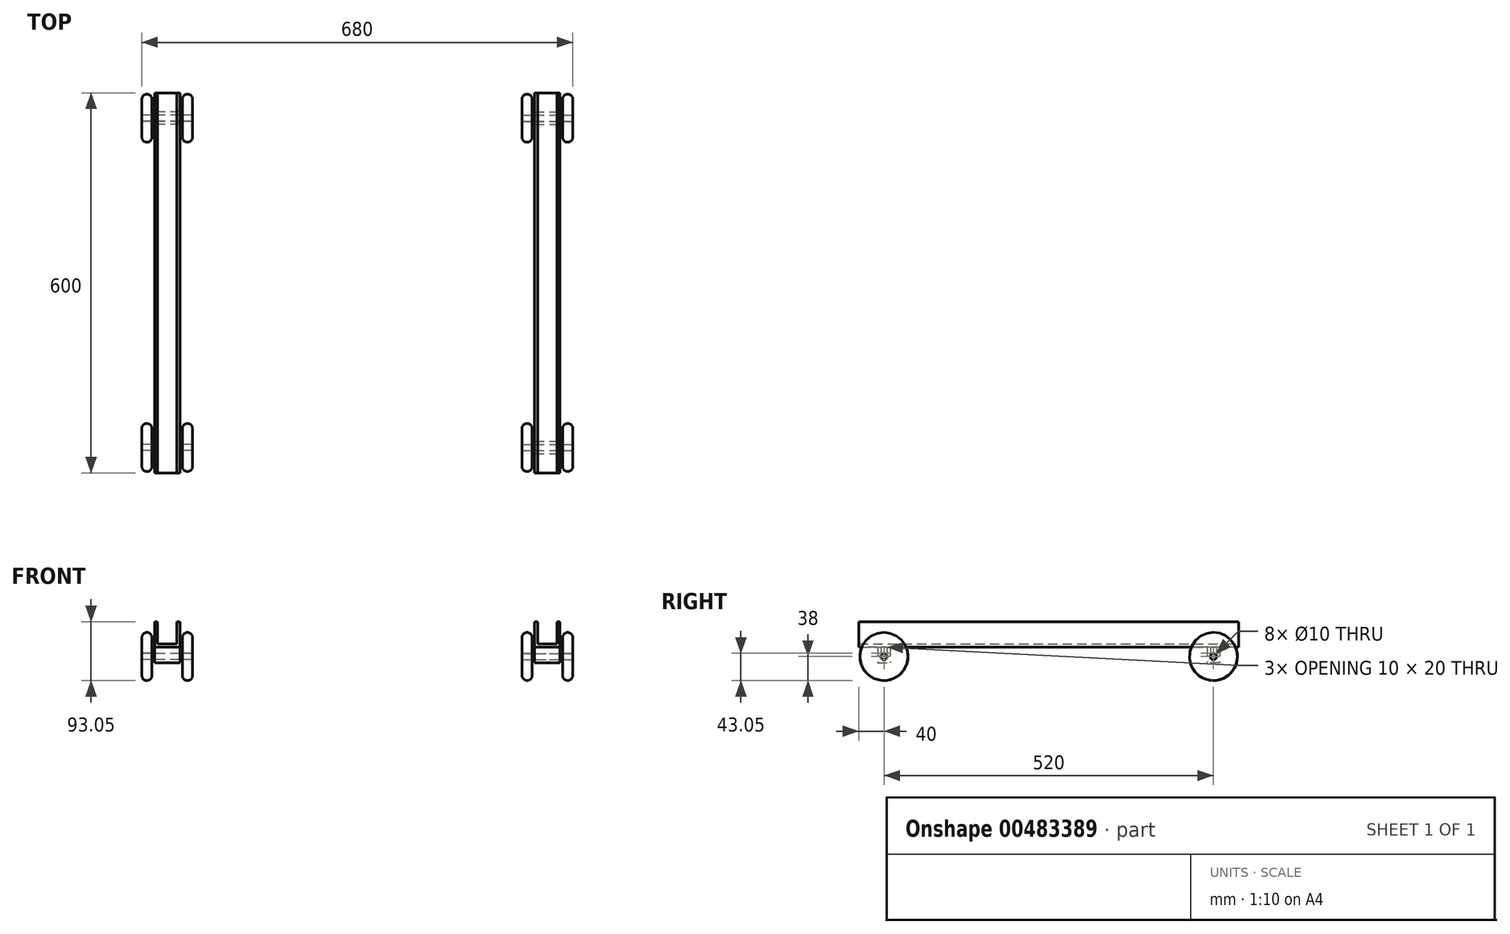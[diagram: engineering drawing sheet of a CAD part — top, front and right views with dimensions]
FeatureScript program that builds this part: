
annotation { "Feature Type Name" : "Feature", "Feature Type Description" : "" }
export const myFeature = defineFeature(function(context is Context, id is Id, definition is map)
    precondition{}
    {
        {
            var Q0;
            Q0=qCreatedBy(makeId("Front.planeOp"),FACE);
            var sketch = newSketch(context, id + "F0", { "sketchPlane" : qUnion([Q0])});
            skLineSegment(sketch, "E0", {"start": v(0, 0) * mm, "end": v(-280, 0) * mm, "construction": true});
            skLineSegment(sketch, "E1.bottom", {"start": v(-280, 0) * mm, "end": v(-320, 0) * mm});
            skLineSegment(sketch, "E1.left", {"start": v(-280, 0) * mm, "end": v(-280, 40) * mm});
            skLineSegment(sketch, "E1.right", {"start": v(-320, 0) * mm, "end": v(-320, 40) * mm});
            skLineSegment(sketch, "E2.0", {"start": v(-315, 5) * mm, "end": v(-315, 40) * mm});
            skLineSegment(sketch, "E2.1", {"start": v(-285, 5) * mm, "end": v(-315, 5) * mm});
            skLineSegment(sketch, "E2.2", {"start": v(-285, 5) * mm, "end": v(-285, 40) * mm});
            skLineSegment(sketch, "E3", {"start": v(-320, 40) * mm, "end": v(-315, 40) * mm});
            skLineSegment(sketch, "E4", {"start": v(-285, 40) * mm, "end": v(-280, 40) * mm});
            skLineSegment(sketch, "E5", {"start": v(0, 0) * mm, "end": v(0, 40) * mm, "construction": true});
            skLineSegment(sketch, "E6.MirrorCS", {"start": v(285, 40) * mm, "end": v(280, 40) * mm});
            skLineSegment(sketch, "E7.MirrorCS", {"start": v(320, 40) * mm, "end": v(315, 40) * mm});
            skLineSegment(sketch, "E8.MirrorCS", {"start": v(315, 5) * mm, "end": v(315, 40) * mm});
            skLineSegment(sketch, "E9.MirrorCS", {"start": v(320, 0) * mm, "end": v(320, 40) * mm});
            skLineSegment(sketch, "E10.MirrorCS", {"start": v(280, 0) * mm, "end": v(320, 0) * mm});
            skLineSegment(sketch, "E11.MirrorCS", {"start": v(280, 0) * mm, "end": v(280, 40) * mm});
            skLineSegment(sketch, "E12.MirrorCS", {"start": v(285, 5) * mm, "end": v(315, 5) * mm});
            skLineSegment(sketch, "E13.MirrorCS", {"start": v(285, 5) * mm, "end": v(285, 40) * mm});
            skSolve(sketch);
        }
        {
            var Q0;
            Q0 = qSketchRegion(id + "F0", true);
            extrude(context, id + "F1", {"entities" : qUnion([Q0]), "depth" : 300 * mm, "hasSecondDirection" : true, "secondDirectionOppositeDirection" : true, "secondDirectionDepth" : 300 * mm});
        }
        {
            var Q0;
            Q0=makeQuery(id+"F1.opExtrude","CAP_EDGE",EDGE,{"disambiguationData":[OSD([sQuery(id+"F0.wireOp",EDGE,"E1.bottom")])],"isStart":true});
            cPoint(context, id + "F2", {"entities" : qUnion([Q0]), "parameter" : 0.5});
        }
        {
            var Q0;
            Q0=qCreatedBy(makeId("Right.planeOp"),FACE);
            var Q1;
            Q1 = qCreatedBy(id + "F2" ,VERTEX);
            cPlane(context, id + "F3", {"entities" : qUnion([Q0, Q1]), "cplaneType" : CPlaneType.PLANE_POINT, "offset" : 25 * mm, "width" : 150 * mm, "height" : 150 * mm});
        }
        {
            var Q0;
            Q0=makeQuery(id+"F1.opExtrude","SWEPT_FACE",FACE,{"disambiguationData":[OSD([sQuery(id+"F0.wireOp",EDGE,"E1.right")])]});
            var sketch = newSketch(context, id + "F4", { "sketchPlane" : qUnion([Q0])});
            skLineSegment(sketch, "E14.bottom", {"start": v(-265, 0) * mm, "end": v(-255, 0) * mm});
            skLineSegment(sketch, "E14.top", {"start": v(-260, -20) * mm, "end": v(-260, -20) * mm});
            skLineSegment(sketch, "E14.left", {"start": v(-265, 0) * mm, "end": v(-265, -15) * mm});
            skLineSegment(sketch, "E14.right", {"start": v(-255, 0) * mm, "end": v(-255, -15) * mm});
            skPoint(sketch, "E15", {"position": v(-260, -20) * mm});
            skPoint(sketch, "E16.visualSharp", {"position": v(-265, -20) * mm});
            skArc(sketch, "E16.filletArc", {"start": v(-265, -15) * mm, "mid": v(-263.54, -18.54) * mm, "end": v(-260, -20) * mm});
            skPoint(sketch, "E17.visualSharp", {"position": v(-255, -20) * mm});
            skArc(sketch, "E17.filletArc", {"start": v(-260, -20) * mm, "mid": v(-256.46, -18.54) * mm, "end": v(-255, -15) * mm});
            skLineSegment(sketch, "E18.bottom", {"start": v(-270, 0) * mm, "end": v(-250, 0) * mm});
            skLineSegment(sketch, "E18.top", {"start": v(-270, -25) * mm, "end": v(-250, -25) * mm});
            skLineSegment(sketch, "E18.left", {"start": v(-270, 0) * mm, "end": v(-270, -25) * mm});
            skLineSegment(sketch, "E18.right", {"start": v(-250, 0) * mm, "end": v(-250, -25) * mm});
            skLineSegment(sketch, "E19", {"start": v(-260, -20) * mm, "end": v(-260, -25) * mm, "construction": true});
            skPoint(sketch, "E19.endSnap0", {"position": v(-260, -25) * mm});
            skSolve(sketch);
        }
        {
            var Q0;
            {var subQ1=sQuery(id+"F4.wireOp",EDGE,"E14.left");Q0=makeQuery(id+"F4.imprint","IMPRINT",FACE,{"disambiguationData":[TD([[makeQuery(id+"F4.imprint","IMPRINT",EDGE,{"derivedFrom":subQ1}),-1.0]])]});}
            var Q1;
            Q1=makeQuery(id+"F1.opExtrude","SWEPT_FACE",FACE,{"disambiguationData":[OSD([sQuery(id+"F0.wireOp",EDGE,"E1.left")])]});
            extrude(context, id + "F5", {"entities" : qUnion([Q0]), "endBound" : BoundingType.UP_TO_SURFACE, "oppositeDirection" : true, "endBoundEntityFace" : qUnion([Q1]), "depth" : 25 * mm});
        }
        {
            var Q0;
            Q0=qCreatedBy(id+"F3.planeOp",FACE);
            var sketch = newSketch(context, id + "F6", { "sketchPlane" : qUnion([Q0])});
            skCircle(sketch, "E20", {"center": v(260, -15.05) * mm, "radius": 4.95 * mm});
            skLineSegment(sketch, "E21", {"start": v(260, -15.05) * mm, "end": v(260, -20) * mm, "construction": true});
            skPoint(sketch, "E22", {"position": v(260, -20) * mm});
            skSolve(sketch);
        }
        {
            var Q0;
            Q0 = qSketchRegion(id + "F6", true);
            extrude(context, id + "F7", {"entities" : qUnion([Q0]), "depth" : 40 * mm, "hasSecondDirection" : true, "secondDirectionOppositeDirection" : true, "secondDirectionDepth" : 40 * mm});
        }
        {
            var Q0;
            Q0=qCreatedBy(makeId("Top.planeOp"),FACE);
            var Q1;
            Q1=sQuery(id+"F6.wireOp",VERTEX,"E20.center");
            cPlane(context, id + "F8", {"entities" : qUnion([Q0, Q1]), "cplaneType" : CPlaneType.PLANE_POINT, "offset" : 25 * mm, "width" : 150 * mm, "height" : 150 * mm});
        }
        {
            var Q0;
            Q0=qCreatedBy(id+"F8.planeOp",FACE);
            var sketch = newSketch(context, id + "F9", { "sketchPlane" : qUnion([Q0])});
            skLineSegment(sketch, "E23", {"start": v(-300, 260) * mm, "end": v(-300, 300) * mm, "construction": true});
            skLineSegment(sketch, "E24", {"start": v(-332, 260) * mm, "end": v(-300, 260) * mm, "construction": true});
            skLineSegment(sketch, "E25", {"start": v(-332, 260) * mm, "end": v(-332, 265) * mm, "construction": true});
            skLineSegment(sketch, "E26", {"start": v(-332, 265) * mm, "end": v(-340, 265) * mm});
            skLineSegment(sketch, "E27", {"start": v(-340, 265) * mm, "end": v(-340, 290) * mm});
            skArc(sketch, "E28", {"start": v(-332, 298) * mm, "mid": v(-337.66, 295.66) * mm, "end": v(-340, 290) * mm});
            skLineSegment(sketch, "E29", {"start": v(-332, 290) * mm, "end": v(-332, 265) * mm, "construction": true});
            skLineSegment(sketch, "E30.MirrorCS", {"start": v(-324, 265) * mm, "end": v(-324, 290) * mm});
            skLineSegment(sketch, "E31.MirrorCS", {"start": v(-332, 265) * mm, "end": v(-324, 265) * mm});
            skArc(sketch, "E32.MirrorCS", {"start": v(-332, 298) * mm, "mid": v(-326.34, 295.66) * mm, "end": v(-324, 290) * mm});
            skLineSegment(sketch, "E33.MirrorCS", {"start": v(-364, 260) * mm, "end": v(-364, 300) * mm, "construction": true});
            skLineSegment(sketch, "E34.MirrorCS", {"start": v(-260, 265) * mm, "end": v(-260, 290) * mm});
            skArc(sketch, "E35.MirrorCS", {"start": v(-268, 298) * mm, "mid": v(-262.34, 295.66) * mm, "end": v(-260, 290) * mm});
            skArc(sketch, "E36.MirrorCS", {"start": v(-268, 298) * mm, "mid": v(-273.66, 295.66) * mm, "end": v(-276, 290) * mm});
            skLineSegment(sketch, "E37.MirrorCS", {"start": v(-276, 265) * mm, "end": v(-276, 290) * mm});
            skLineSegment(sketch, "E38.MirrorCS", {"start": v(-268, 265) * mm, "end": v(-276, 265) * mm});
            skLineSegment(sketch, "E39.MirrorCS", {"start": v(-268, 265) * mm, "end": v(-260, 265) * mm});
            skSolve(sketch);
        }
        {
            var Q0;
            Q0=makeQuery(id+"F9.imprint","IMPRINT",FACE,{"disambiguationData":[TD([[makeQuery(id+"F9.imprint","IMPRINT",EDGE,{"derivedFrom":sQuery(id+"F9.wireOp",EDGE,"E31.MirrorCS")}),1.0]])]});
            var Q1;
            Q1=makeQuery(id+"F9.imprint","IMPRINT",FACE,{"disambiguationData":[TD([[makeQuery(id+"F9.imprint","IMPRINT",EDGE,{"derivedFrom":sQuery(id+"F9.wireOp",EDGE,"E34.MirrorCS")}),1.0]])]});
            var Q2;
            Q2=sQuery(id+"F9.wireOp",EDGE,"E24");
            revolve(context, id + "F10", {"entities" : qUnion([Q0, Q1]), "axis" : qUnion([Q2]), "revolveType" : RevolveType.FULL});
        }
        {
            var Q0;
            Q0=makeQuery(id+"F5.opExtrude","SWEPT_BODY",BODY,{"disambiguationData":[OSD([sQuery(id+"F4.wireOp",EDGE,"E14.left"),sQuery(id+"F4.wireOp",EDGE,"E14.right"),sQuery(id+"F4.wireOp",EDGE,"E16.filletArc"),sQuery(id+"F4.wireOp",EDGE,"E17.filletArc"),sQuery(id+"F4.wireOp",EDGE,"E18.bottom"),sQuery(id+"F4.wireOp",EDGE,"E18.top"),sQuery(id+"F4.wireOp",EDGE,"E18.left"),sQuery(id+"F4.wireOp",EDGE,"E18.right")])]});
            var Q1;
            Q1=makeQuery(id+"F10.opRevolve","SWEPT_BODY",BODY,{"disambiguationData":[OSD([sQuery(id+"F9.wireOp",EDGE,"E31.MirrorCS"),sQuery(id+"F9.wireOp",EDGE,"E28"),sQuery(id+"F9.wireOp",EDGE,"E30.MirrorCS"),sQuery(id+"F9.wireOp",EDGE,"E26"),sQuery(id+"F9.wireOp",EDGE,"E27"),sQuery(id+"F9.wireOp",EDGE,"E32.MirrorCS")])]});
            var Q2;
            Q2=makeQuery(id+"F7.opExtrude","SWEPT_BODY",BODY,{"disambiguationData":[OSD([sQuery(id+"F6.wireOp",EDGE,"E20")])]});
            var Q3;
            Q3=makeQuery(id+"F10.opRevolve","SWEPT_BODY",BODY,{"disambiguationData":[OSD([sQuery(id+"F9.wireOp",EDGE,"E34.MirrorCS"),sQuery(id+"F9.wireOp",EDGE,"E35.MirrorCS"),sQuery(id+"F9.wireOp",EDGE,"E36.MirrorCS"),sQuery(id+"F9.wireOp",EDGE,"E37.MirrorCS"),sQuery(id+"F9.wireOp",EDGE,"E38.MirrorCS"),sQuery(id+"F9.wireOp",EDGE,"E39.MirrorCS")])]});
            var Q4;
            Q4=qCreatedBy(makeId("Right.planeOp"),FACE);
            mirror(context, id + "F11", {"operationType" : NewBodyOperationType.ADD, "entities" : qUnion([Q0, Q1, Q2, Q3]), "mirrorPlane" : qUnion([Q4])});
        }
        {
            var Q0;
            Q0=makeQuery(id+"F5.opExtrude","SWEPT_BODY",BODY,{"disambiguationData":[OSD([sQuery(id+"F4.wireOp",EDGE,"E14.left"),sQuery(id+"F4.wireOp",EDGE,"E14.right"),sQuery(id+"F4.wireOp",EDGE,"E16.filletArc"),sQuery(id+"F4.wireOp",EDGE,"E17.filletArc"),sQuery(id+"F4.wireOp",EDGE,"E18.bottom"),sQuery(id+"F4.wireOp",EDGE,"E18.top"),sQuery(id+"F4.wireOp",EDGE,"E18.left"),sQuery(id+"F4.wireOp",EDGE,"E18.right")])]});
            var Q1;
            Q1=makeQuery(id+"F1.opExtrude","SWEPT_BODY",BODY,{"disambiguationData":[OSD([sQuery(id+"F0.wireOp",EDGE,"E6.MirrorCS"),sQuery(id+"F0.wireOp",EDGE,"E7.MirrorCS"),sQuery(id+"F0.wireOp",EDGE,"E13.MirrorCS"),sQuery(id+"F0.wireOp",EDGE,"E12.MirrorCS"),sQuery(id+"F0.wireOp",EDGE,"E11.MirrorCS"),sQuery(id+"F0.wireOp",EDGE,"E9.MirrorCS"),sQuery(id+"F0.wireOp",EDGE,"E10.MirrorCS"),sQuery(id+"F0.wireOp",EDGE,"E8.MirrorCS")])]});
            var Q2;
            Q2=makeQuery(id+"F11.opPattern","COPY",BODY,{"derivedFrom":makeQuery(id+"F10.opRevolve","SWEPT_BODY",BODY,{"disambiguationData":[OSD([sQuery(id+"F9.wireOp",EDGE,"E34.MirrorCS"),sQuery(id+"F9.wireOp",EDGE,"E35.MirrorCS"),sQuery(id+"F9.wireOp",EDGE,"E36.MirrorCS"),sQuery(id+"F9.wireOp",EDGE,"E37.MirrorCS"),sQuery(id+"F9.wireOp",EDGE,"E38.MirrorCS"),sQuery(id+"F9.wireOp",EDGE,"E39.MirrorCS")])]}),"instanceName":"1"});
            var Q3;
            Q3=makeQuery(id+"F11.boolean.opBoolean","MERGE",BODY,{"derivedFrom":[makeQuery(id+"F11.opPattern","COPY",BODY,{"derivedFrom":makeQuery(id+"F5.opExtrude","SWEPT_BODY",BODY,{"disambiguationData":[OSD([sQuery(id+"F4.wireOp",EDGE,"E14.left"),sQuery(id+"F4.wireOp",EDGE,"E14.right"),sQuery(id+"F4.wireOp",EDGE,"E16.filletArc"),sQuery(id+"F4.wireOp",EDGE,"E17.filletArc"),sQuery(id+"F4.wireOp",EDGE,"E18.bottom"),sQuery(id+"F4.wireOp",EDGE,"E18.top"),sQuery(id+"F4.wireOp",EDGE,"E18.left"),sQuery(id+"F4.wireOp",EDGE,"E18.right")])]}),"instanceName":"1"}),makeQuery(id+"F11.opPattern","COPY",BODY,{"derivedFrom":makeQuery(id+"F7.opExtrude","SWEPT_BODY",BODY,{"disambiguationData":[OSD([sQuery(id+"F6.wireOp",EDGE,"E20")])]}),"instanceName":"1"})]});
            var Q4;
            Q4=makeQuery(id+"F11.opPattern","COPY",BODY,{"derivedFrom":makeQuery(id+"F10.opRevolve","SWEPT_BODY",BODY,{"disambiguationData":[OSD([sQuery(id+"F9.wireOp",EDGE,"E31.MirrorCS"),sQuery(id+"F9.wireOp",EDGE,"E28"),sQuery(id+"F9.wireOp",EDGE,"E30.MirrorCS"),sQuery(id+"F9.wireOp",EDGE,"E26"),sQuery(id+"F9.wireOp",EDGE,"E27"),sQuery(id+"F9.wireOp",EDGE,"E32.MirrorCS")])]}),"instanceName":"1"});
            var Q5;
            Q5=makeQuery(id+"F10.opRevolve","SWEPT_BODY",BODY,{"disambiguationData":[OSD([sQuery(id+"F9.wireOp",EDGE,"E31.MirrorCS"),sQuery(id+"F9.wireOp",EDGE,"E28"),sQuery(id+"F9.wireOp",EDGE,"E30.MirrorCS"),sQuery(id+"F9.wireOp",EDGE,"E26"),sQuery(id+"F9.wireOp",EDGE,"E27"),sQuery(id+"F9.wireOp",EDGE,"E32.MirrorCS")])]});
            var Q6;
            Q6=makeQuery(id+"F10.opRevolve","SWEPT_BODY",BODY,{"disambiguationData":[OSD([sQuery(id+"F9.wireOp",EDGE,"E34.MirrorCS"),sQuery(id+"F9.wireOp",EDGE,"E35.MirrorCS"),sQuery(id+"F9.wireOp",EDGE,"E36.MirrorCS"),sQuery(id+"F9.wireOp",EDGE,"E37.MirrorCS"),sQuery(id+"F9.wireOp",EDGE,"E38.MirrorCS"),sQuery(id+"F9.wireOp",EDGE,"E39.MirrorCS")])]});
            var Q7;
            Q7=qCreatedBy(makeId("Front.planeOp"),FACE);
            mirror(context, id + "F12", {"entities" : qUnion([Q0, Q1, Q2, Q3, Q4, Q5, Q6]), "mirrorPlane" : qUnion([Q7])});
        }
    });
